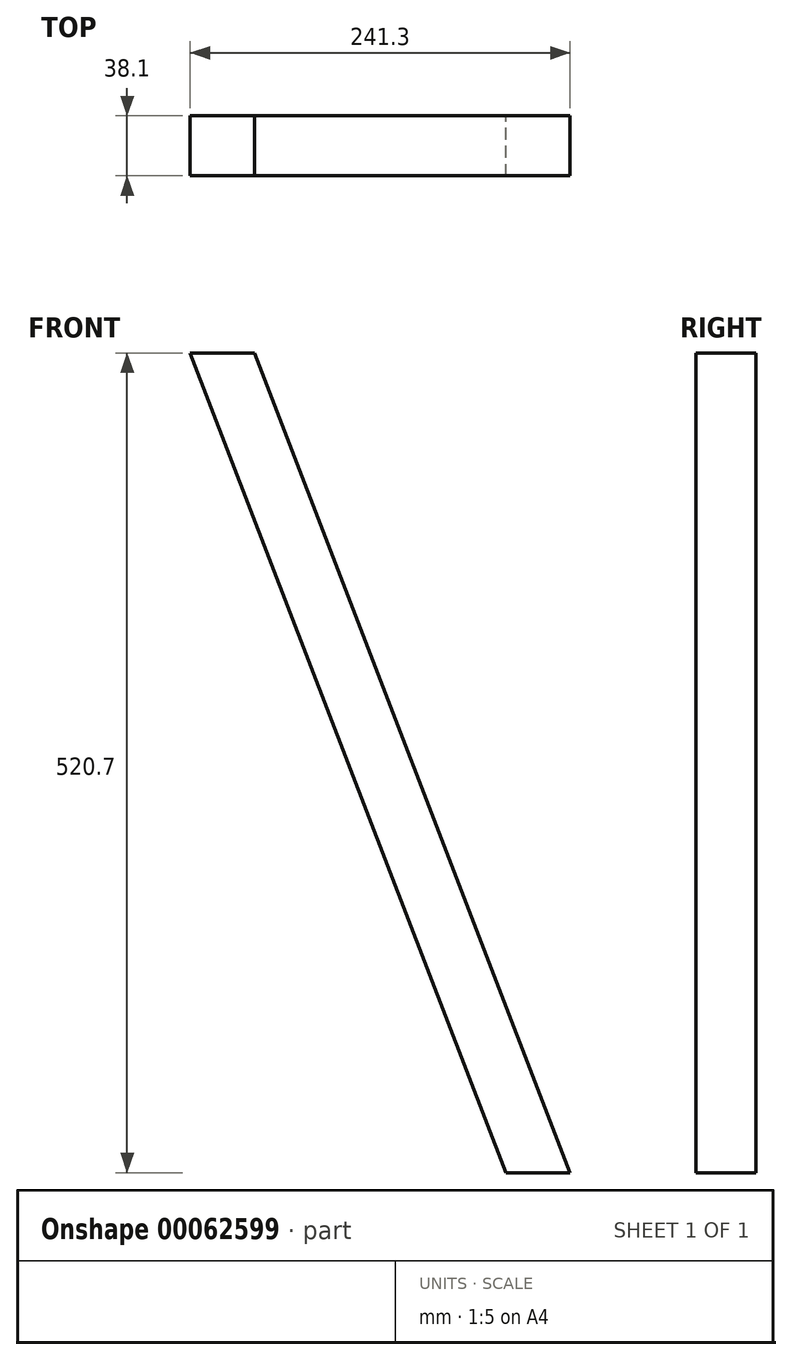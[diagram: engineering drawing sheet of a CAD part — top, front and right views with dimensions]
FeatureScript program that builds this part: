
annotation { "Feature Type Name" : "Feature", "Feature Type Description" : "" }
export const myFeature = defineFeature(function(context is Context, id is Id, definition is map)
    precondition{}
    {
        {
            var Q0;
            Q0=qCreatedBy(makeId("Front.planeOp"),FACE);
            var sketch = newSketch(context, id + "F0", { "sketchPlane" : qUnion([Q0])});
            skLineSegment(sketch, "E0", {"start": v(0, 0) * mm, "end": v(40.83, 0) * mm});
            skLineSegment(sketch, "E1", {"start": v(40.83, 0) * mm, "end": v(241.3, -520.7) * mm});
            skLineSegment(sketch, "E2", {"start": v(241.3, -520.7) * mm, "end": v(200.47, -520.7) * mm});
            skLineSegment(sketch, "E3", {"start": v(200.47, -520.7) * mm, "end": v(0, 0) * mm});
            skSolve(sketch);
        }
        {
            var Q0;
            Q0=makeQuery(id+"F0.imprint","IMPRINT",FACE,{"disambiguationData":[TD([[makeQuery(id+"F0.imprint","IMPRINT",EDGE,{"derivedFrom":sQuery(id+"F0.wireOp",EDGE,"E0")}),-1.0]])]});
            extrude(context, id + "F1", {"entities" : qUnion([Q0]), "depth" : 38.1 * mm});
        }
    });
